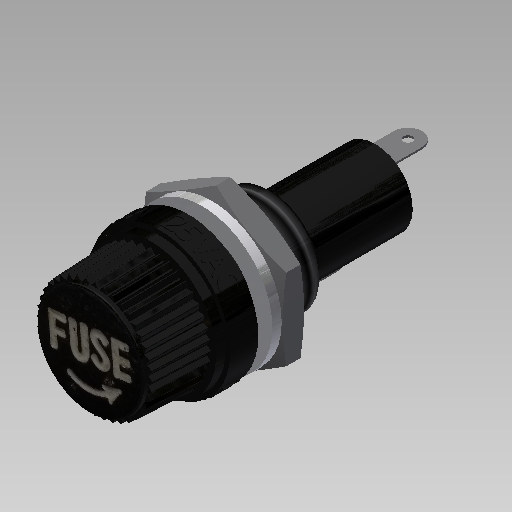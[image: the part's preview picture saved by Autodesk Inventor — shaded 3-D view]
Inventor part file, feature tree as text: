
AUTODESK INVENTOR PART (.ipt)
format: ipt  version: 2020 (Build 240168000, 168)  size: 3,027,968 bytes
history: native  units: mm
features: other x10, extrude x9, fillet x3, sketch x3, sweep x2, hole x2, loft x1, pattern_circular x1, chamfer x1, thread x1, revolve x1, projected_geometry x1
ambient origin geometry x8: Origin, YZ Plane, XZ Plane, XY Plane, X Axis, Y Axis, Z Axis, Center Point
bodies: Body1 (feature_tree)
feature tree (35):
  other  "Твердое тело1"
  extrude  "Выдавливание1"  Depth=11.5mm
  other  "РабПлоскость1"
  loft  "По сечениям1"
  extrude  "Выдавливание2"  Depth=6.0mm
  sweep  "Сдвиг1"
  extrude  "Выдавливание3"  TaperAngle=0.0deg  [1 undecoded]
  other  "Маркировка1"
  fillet  "Сопряжение1"  [1 undecoded]
  pattern_circular  "Круговой массив2"  [2 undecoded]
  extrude  "Выдавливание4"  Depth=1.0mm TaperAngle=0.0deg
  extrude  "Выдавливание5"  Depth=0.5mm
  chamfer  "Фаска1"  Distance=0.8mm
  thread  "Резьба1"
  extrude  "Выдавливание6"  Depth=0.08mm
  extrude  "Выдавливание7"  Depth=0.1mm
  fillet  "Сопряжение2"  [1 undecoded]
  hole  "Отверстие1"  [1 undecoded]
  sweep  "Сдвиг2"
  fillet  "Сопряжение3"  Radius=0.2mm
  hole  "Отверстие2"  [1 undecoded]
  other  "РабПлоскость2"
  extrude  "Выдавливание8"  Depth=11.0mm
  extrude  "Выдавливание9"  Depth=9.0mm TaperAngle=0.0deg
  revolve  "Вращение1"
  other  "РабПлоскость3"
  other  "Рельеф1"
  other  "РабПлоскость4"
  other  "Рельеф2"
  other  "Ребра1"
  projected_geometry  "Спроецированная петля1"
  sketch  "Эскиз8"
  other  "Картинка1"
  sketch  "Эскиз18"
  sketch  "Эскиз19"
note: 7 required parameter values undecoded (feature->parameter linkage not recoverable at this tier; creation-order binding heuristic only, values carry confidence <= 0.55)
